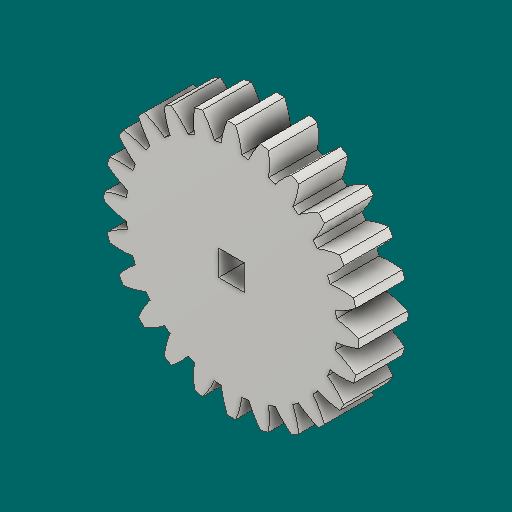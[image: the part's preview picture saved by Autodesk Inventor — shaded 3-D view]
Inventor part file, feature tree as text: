
AUTODESK INVENTOR PART (.ipt)
format: ipt  version: 2023.1 (Build 271208000, 208)  size: 282,624 bytes
history: native  units: in
note: dims shown in document units (in); Inventor stores cm internally (conversion verified against a paired STEP export)
features: other x12, sketch x3, plane x3
ambient origin geometry x8: Origin, YZ Plane, XZ Plane, XY Plane, X Axis, Y Axis, Z Axis, Center Point
bodies: Solid1 (feature_tree)
feature tree (18):
  other  "Spur Gear1"
  other  "Solid1::Spur Gear1"
  other  "TaggingFeature1"
  sketch  "Sketch1"  dims[d0=0.3937in]
  sketch  "Sketch2"  dims[d9=0.0in]
  sketch  "Sketch3"  dims[d14=0.0in d15=1.2in d16=0.0in d17=0.0in d18=0.0in d19=1.2in]
  plane  "XZ Plane_1"
  plane  "Work Plane2"
  plane  "Work Plane3"
  other  "Srf1"
  other  "Srf1::Derived"
  other  "Start plane iMate"
  other  "Distance iMate"
  other  "Position iMate"
  other  "Mesh iMate"
  other  "Axis iMate"
  other  "Mesh iMate2"
  other  "Align iMate"
